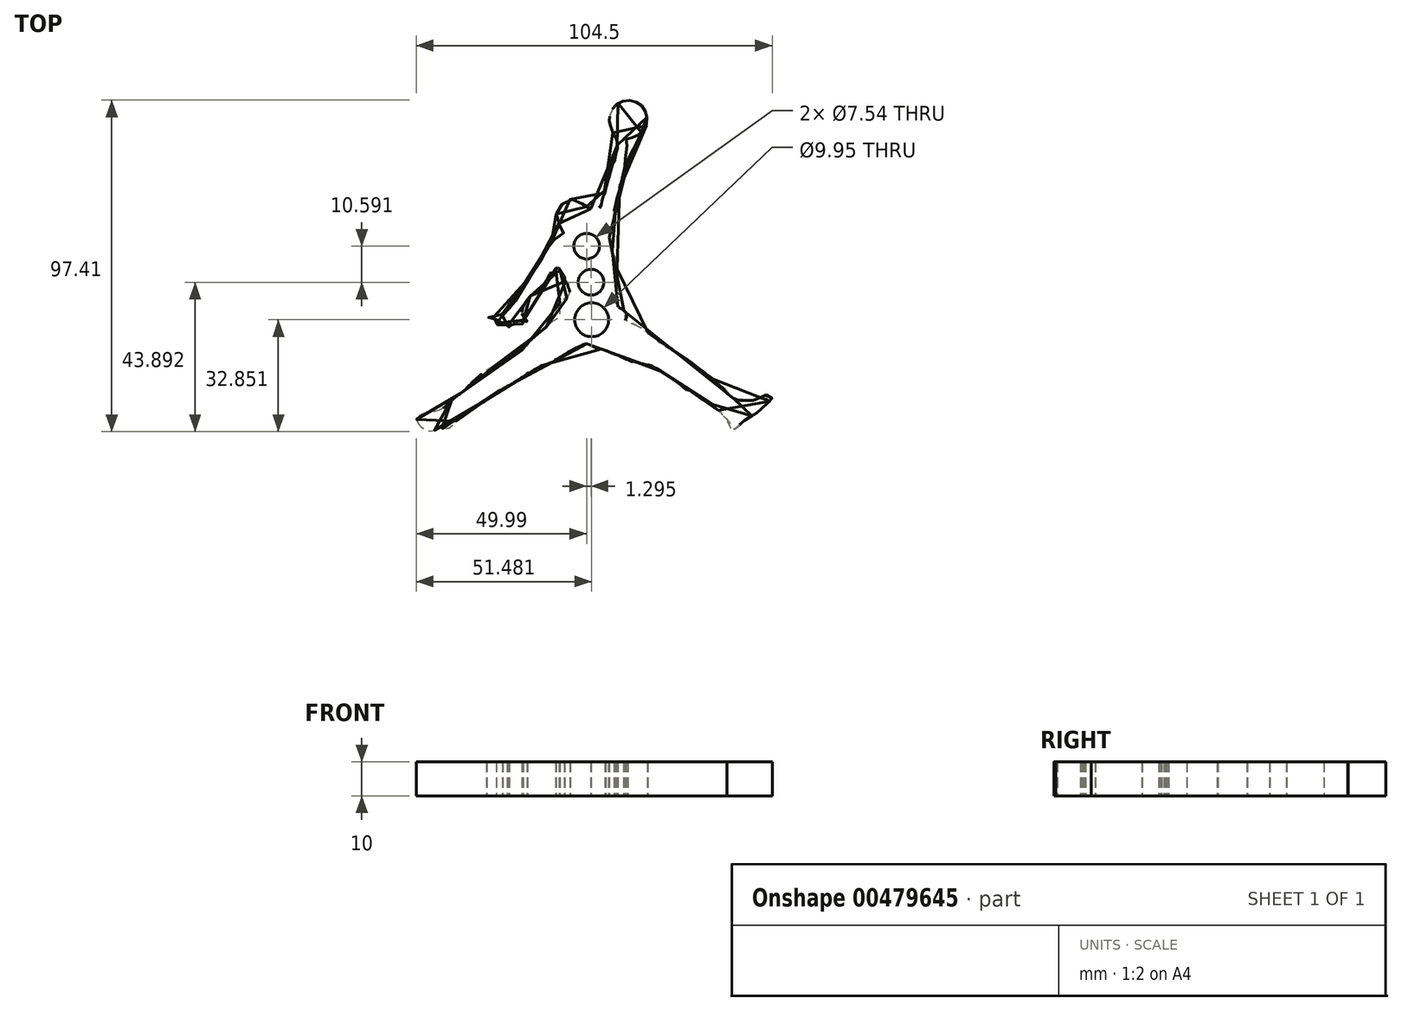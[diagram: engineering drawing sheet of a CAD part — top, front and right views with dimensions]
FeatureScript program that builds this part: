
annotation { "Feature Type Name" : "Feature", "Feature Type Description" : "" }
export const myFeature = defineFeature(function(context is Context, id is Id, definition is map)
    precondition{}
    {
        {
            var Q0;
            Q0=qCreatedBy(makeId("Top.planeOp"),FACE);
            var sketch = newSketch(context, id + "F0", { "sketchPlane" : qUnion([Q0])});
            skFitSpline(sketch, "E0", {"points": [v(0, -19.8) * mm, v(0.2, -19.83) * mm, v(0.48, -19.99) * mm, v(1.1, -20.32) * mm, v(2.32, -20.88) * mm, v(3.56, -21.27) * mm, v(5.27, -21.74) * mm, v(7.68, -22.78) * mm, v(9.68, -23.51) * mm, v(11.32, -24.32) * mm, v(13.95, -25.3) * mm, v(15.3, -25.56) * mm, v(18.19, -26.14) * mm, v(19.48, -26.44) * mm, v(19.57, -26.65) * mm, v(20.06, -26.91) * mm, v(21.05, -27.34) * mm, v(22.12, -27.94) * mm, v(23.74, -29.2) * mm, v(25.71, -30.67) * mm, v(27.3, -31.83) * mm, v(28.82, -33.03) * mm, v(29.33, -33.3) * mm, v(29.66, -33.44) * mm, v(30.19, -33.56) * mm, v(30.42, -33.56) * mm, v(31.1, -34.2) * mm, v(32.19, -34.96) * mm, v(33.13, -35.66) * mm, v(34.06, -36.37) * mm, v(34.75, -36.83) * mm, v(35.13, -36.98) * mm, v(35.58, -36.98) * mm, v(35.91, -36.98) * mm, v(36.16, -36.98) * mm, v(36.7, -37.44) * mm, v(37.25, -37.84) * mm, v(37.4, -38.04) * mm, v(37.53, -38.3) * mm, v(37.79, -38.55) * mm, v(38.11, -38.88) * mm, v(38.42, -39.16) * mm, v(38.8, -39.59) * mm, v(39.15, -39.72) * mm, v(39.3, -40) * mm, v(39.44, -40.32) * mm, v(40.42, -41.42) * mm, v(40.69, -41.76) * mm, v(41.12, -42) * mm, v(41.13, -42.31) * mm, v(41.37, -42.96) * mm, v(41.75, -43.62) * mm, v(42.58, -45) * mm, v(43.18, -45) * mm, v(44.19, -44.26) * mm, v(45.57, -43.07) * mm, v(47.18, -41.78) * mm, v(49.3, -40.67) * mm, v(51.32, -39.06) * mm, v(52.93, -37.54) * mm, v(54.5, -35.98) * mm, v(54.31, -35.5) * mm, v(53.92, -35.14) * mm, v(53.48, -34.9) * mm, v(52.87, -34.71) * mm, v(52.07, -34.83) * mm, v(51.46, -35.2) * mm, v(50.72, -35.63) * mm, v(50.03, -36.06) * mm, v(49.52, -36.26) * mm, v(48.35, -36.32) * mm, v(46.9, -36.34) * mm, v(45.76, -36.31) * mm, v(44.32, -36.3) * mm, v(43.12, -35.83) * mm, v(42.05, -34.72) * mm, v(41.47, -34.5) * mm, v(41.02, -34.03) * mm, v(40.88, -33.43) * mm, v(40.56, -33) * mm, v(39.17, -32.11) * mm, v(37.3, -30.2) * mm, v(36.82, -29.96) * mm, v(35.4, -28.76) * mm, v(33.62, -27.29) * mm, v(31.48, -25.76) * mm, v(29, -23.88) * mm, v(27.27, -22.71) * mm, v(25.08, -21.3) * mm, v(23.68, -20.35) * mm, v(23.38, -20.22) * mm, v(22.62, -20.12) * mm, v(21.98, -19.97) * mm, v(20.96, -18.83) * mm, v(19.69, -17.68) * mm, v(18.54, -16.8) * mm, v(17.36, -15.88) * mm, v(15.82, -14.96) * mm, v(14.2, -14.23) * mm, v(13, -13.6) * mm, v(11.37, -12.78) * mm, v(11.5, -12.6) * mm, v(11.63, -12.33) * mm, v(11.73, -12.03) * mm, v(11.78, -11.66) * mm, v(11.78, -11.43) * mm, v(11.72, -11.1) * mm, v(11.47, -10.57) * mm, v(11.04, -10.14) * mm, v(10.46, -9.65) * mm, v(9.6, -9.16) * mm, v(9.23, -9.02) * mm, v(8.92, -8.2) * mm, v(8.4, -7.03) * mm, v(8.55, -6.5) * mm, v(8.93, -4.45) * mm, v(9.15, -2.65) * mm, v(9.15, -0.27) * mm, v(9.04, 3.33) * mm, v(8.75, 5.3) * mm, v(7.8, 6.92) * mm, v(7.17, 8.5) * mm, v(6.73, 10.55) * mm, v(6.7, 11.32) * mm, v(6.63, 12.71) * mm, v(6.92, 13.58) * mm, v(7.53, 15) * mm, v(7.96, 16.47) * mm, v(8.12, 17.37) * mm, v(8.18, 18.32) * mm, v(8.17, 19) * mm, v(8.19, 19.73) * mm, v(8.4, 20.15) * mm, v(8.63, 20.9) * mm, v(8.65, 21.68) * mm, v(8.69, 22.57) * mm, v(9.04, 23.14) * mm, v(9.28, 23.9) * mm, v(9.63, 25.04) * mm, v(10.14, 27.67) * mm, v(10.56, 28.03) * mm, v(10.97, 28.41) * mm, v(10.97, 29.06) * mm, v(11.35, 30.86) * mm, v(11.47, 32.16) * mm, v(11.26, 32.93) * mm, v(11.38, 34.34) * mm, v(11.55, 35.53) * mm, v(11.75, 36.87) * mm, v(11.8, 37.9) * mm, v(12.08, 38.72) * mm, v(12.08, 39.7) * mm, v(11.8, 40.14) * mm, v(11.77, 40.47) * mm, v(11.97, 40.67) * mm, v(12.41, 40.67) * mm, v(13.83, 40.86) * mm, v(15.35, 41.58) * mm, v(16.46, 42.42) * mm, v(17.28, 43.69) * mm, v(17.85, 45.37) * mm, v(17.85, 46.66) * mm, v(17.7, 47.76) * mm, v(16.45, 50) * mm, v(14.85, 51.2) * mm, v(13.17, 51.76) * mm, v(11.4, 51.72) * mm, v(9.32, 51) * mm, v(7.84, 49.76) * mm, v(7.04, 48.07) * mm, v(6.52, 46.47) * mm, v(6.8, 44.8) * mm, v(7.12, 43.59) * mm, v(7.52, 42.5) * mm, v(7.92, 41.63) * mm, v(8.48, 40.63) * mm, v(8.8, 39.59) * mm, v(9, 38.7) * mm, v(8.8, 37.22) * mm, v(8.32, 35.02) * mm, v(8, 33.7) * mm, v(7.64, 33.68) * mm, v(7.49, 33.28) * mm, v(6.98, 31.54) * mm, v(6.42, 29.74) * mm, v(6.4, 29.36) * mm, v(6.52, 29.25) * mm, v(6.28, 28.69) * mm, v(5.8, 27.72) * mm, v(5.47, 26.9) * mm, v(5.43, 25.97) * mm, v(5.5, 25.32) * mm, v(4.93, 23.98) * mm, v(4.28, 21.56) * mm, v(3.93, 20.36) * mm, v(2.62, 19.25) * mm, v(1.97, 17.75) * mm, v(1.83, 18.14) * mm, v(1.6, 18.68) * mm, v(1.35, 18.93) * mm, v(1.25, 19.12) * mm, v(1.26, 19.84) * mm, v(1.16, 20) * mm, v(0.85, 20.1) * mm, v(0, 20.35) * mm, v(-0.12, 20.4) * mm, v(-0.3, 20.79) * mm, v(-0.65, 20.9) * mm, v(-0.93, 21) * mm, v(-1.4, 21.55) * mm, v(-2.02, 22.07) * mm, v(-2.8, 22.45) * mm, v(-3.7, 22.65) * mm, v(-4.58, 22.65) * mm, v(-5.6, 22.44) * mm, v(-5.99, 22.27) * mm, v(-6.86, 21.68) * mm, v(-7.56, 20.92) * mm, v(-8.27, 19.95) * mm, v(-9, 18.2) * mm, v(-8.94, 16.83) * mm, v(-8.44, 15.6) * mm, v(-7.7, 14.82) * mm, v(-7, 14.19) * mm, v(-6.7, 13.85) * mm, v(-6.6, 13.68) * mm, v(-6.76, 13.45) * mm, v(-6.84, 12.99) * mm, v(-6.96, 12.6) * mm, v(-7.42, 12.08) * mm, v(-8.13, 11.5) * mm, v(-8.53, 11.19) * mm, v(-8.97, 11.19) * mm, v(-9.5, 10.92) * mm, v(-10.2, 10.58) * mm, v(-10.93, 9.51) * mm, v(-11.95, 7.84) * mm, v(-12.98, 6.05) * mm, v(-13.52, 4.9) * mm, v(-13.7, 4.78) * mm, v(-14.25, 4.13) * mm, v(-14.77, 3.23) * mm, v(-15.14, 2.47) * mm, v(-15.35, 1.54) * mm, v(-15.93, 1.12) * mm, v(-17.56, -1.04) * mm, v(-18.35, -2.14) * mm, v(-19.01, -3.42) * mm, v(-20.12, -5.37) * mm, v(-20.55, -6.26) * mm, v(-20.93, -7.15) * mm, v(-21.08, -7.54) * mm, v(-21.83, -8.35) * mm, v(-22.7, -9.2) * mm, v(-23.65, -10.32) * mm, v(-25.58, -11.33) * mm, v(-26.46, -11.67) * mm, v(-28.16, -11.97) * mm, v(-29.17, -11.95) * mm, v(-29.43, -12.14) * mm, v(-29.32, -12.52) * mm, v(-29, -12.68) * mm, v(-27.78, -12.87) * mm, v(-26.67, -12.85) * mm, v(-25.56, -12.66) * mm, v(-24.78, -12.47) * mm, v(-24.7, -12.59) * mm, v(-24.87, -12.85) * mm, v(-25.4, -13.1) * mm, v(-25.98, -13.34) * mm, v(-26.48, -13.58) * mm, v(-26.53, -14) * mm, v(-26.24, -14.29) * mm, v(-25.72, -14.29) * mm, v(-24.7, -13.98) * mm, v(-23.6, -13.65) * mm, v(-22.87, -13.37) * mm, v(-22.96, -13.82) * mm, v(-23.2, -14.24) * mm, v(-23.36, -14.69) * mm, v(-23.05, -14.93) * mm, v(-22.32, -14.76) * mm, v(-21.54, -13.82) * mm, v(-20.95, -13.23) * mm, v(-20.53, -12.99) * mm, v(-20.12, -13.18) * mm, v(-19.86, -13.58) * mm, v(-19.18, -13.89) * mm, v(-18.45, -14) * mm, v(-17.79, -14) * mm, v(-17.43, -13.72) * mm, v(-17.38, -13.3) * mm, v(-17.64, -13.01) * mm, v(-18.33, -12.87) * mm, v(-18.7, -12.54) * mm, v(-18.92, -12) * mm, v(-18.68, -11.57) * mm, v(-18.87, -10.93) * mm, v(-18.85, -9.99) * mm, v(-18.42, -8.8) * mm, v(-17.71, -7.37) * mm, v(-17.02, -6.38) * mm, v(-16.6, -5.89) * mm, v(-15.45, -5.26) * mm, v(-13.94, -3.96) * mm, v(-12.68, -2.73) * mm, v(-11.66, -1.05) * mm, v(-10.86, 0.42) * mm, v(-10.74, 0.83) * mm, v(-10.32, 0.94) * mm, v(-9.56, 1.34) * mm, v(-9.27, 1.78) * mm, v(-8.99, 2.36) * mm, v(-8.7, 2.32) * mm, v(-8.16, 2.3) * mm, v(-7.93, 2.01) * mm, v(-7.62, 1.44) * mm, v(-7.2, 0.76) * mm, v(-6.8, 0.19) * mm, v(-6.56, -0.15) * mm, v(-6.51, -0.63) * mm, v(-6.5, -1.2) * mm, v(-6.23, -1.5) * mm, v(-5.87, -2) * mm, v(-5.69, -2.18) * mm, v(-5.6, -2.7) * mm, v(-5.39, -3.44) * mm, v(-5.2, -4.1) * mm, v(-4.96, -4.71) * mm, v(-4.88, -5.07) * mm, v(-5.35, -5.55) * mm, v(-5.75, -6.2) * mm, v(-5.9, -6.54) * mm, v(-6.45, -6.58) * mm, v(-6.95, -6.78) * mm, v(-7.52, -7.26) * mm, v(-7.82, -7.89) * mm, v(-8.02, -8.63) * mm, v(-8.02, -9.27) * mm, v(-8.07, -11.5) * mm, v(-8.53, -12.18) * mm, v(-9.13, -12.78) * mm, v(-9.73, -13.06) * mm, v(-10.45, -13.22) * mm, v(-10.95, -13.6) * mm, v(-11.33, -14.19) * mm, v(-11.53, -14.49) * mm, v(-12.87, -15.47) * mm, v(-14.13, -16.47) * mm, v(-15.42, -17.68) * mm, v(-16.6, -19.1) * mm, v(-17.56, -20.03) * mm, v(-18.21, -21.16) * mm, v(-18.58, -21.64) * mm, v(-18.96, -21.75) * mm, v(-19.47, -21.82) * mm, v(-20.07, -22.02) * mm, v(-20.92, -22.52) * mm, v(-21.49, -23.06) * mm, v(-21.94, -23.46) * mm, v(-24.7, -24.7) * mm, v(-28.08, -26.7) * mm, v(-30.64, -28.42) * mm, v(-32.43, -29.87) * mm, v(-33.58, -30.95) * mm, v(-35.47, -32.92) * mm, v(-36.76, -34.15) * mm, v(-38.14, -35.01) * mm, v(-39.62, -36.3) * mm, v(-40.97, -37.56) * mm, v(-42.2, -38.67) * mm, v(-43.45, -39.22) * mm, v(-44.68, -39.65) * mm, v(-45.7, -39.83) * mm, v(-46.8, -40.02) * mm, v(-48.3, -40.26) * mm, v(-49.8, -41.48) * mm, v(-49.93, -42.56) * mm, v(-49.26, -43.64) * mm, v(-47.97, -44.8) * mm, v(-46.76, -45.47) * mm, v(-44.93, -45.47) * mm, v(-43.58, -44.86) * mm, v(-42.36, -44.66) * mm, v(-41.07, -44.66) * mm, v(-39.86, -44.39) * mm, v(-38.98, -43.3) * mm, v(-38.37, -42.56) * mm, v(-37.76, -42.3) * mm, v(-37.02, -41.75) * mm, v(-36.27, -40.26) * mm, v(-35.33, -39.86) * mm, v(-34.51, -38.98) * mm, v(-33.77, -38.57) * mm, v(-32.55, -37.9) * mm, v(-32.14, -37.58) * mm, v(-31.84, -37.74) * mm, v(-31.3, -37.86) * mm, v(-30.89, -37.67) * mm, v(-30.39, -37.22) * mm, v(-25.67, -33.66) * mm, v(-25, -33.4) * mm, v(-22.17, -31.83) * mm, v(-19.98, -30.47) * mm, v(-17.05, -28.43) * mm, v(-15.38, -27.23) * mm, v(-13.6, -26.45) * mm, v(-9.74, -24.72) * mm, v(-7.28, -23.42) * mm, v(-4.62, -21.74) * mm, v(-2.1, -20.54) * mm, v(-0.7, -19.91) * mm, v(0, -19.8) * mm]});
            skCircle(sketch, "E1", {"center": v(0, 8.9) * mm, "radius": 3.67 * mm});
            skCircle(sketch, "E2", {"center": v(1.5, -12.74) * mm, "radius": 4.88 * mm});
            skCircle(sketch, "E3", {"center": v(1.3, -1.7) * mm, "radius": 3.67 * mm});
            skSolve(sketch);
        }
        {
            var Q0;
            Q0=makeQuery(id+"F0.imprint","IMPRINT",FACE,{"disambiguationData":[TD([[makeQuery(id+"F0.imprint","IMPRINT",EDGE,{"derivedFrom":sQuery(id+"F0.wireOp",EDGE,"E0")}),1.0]])]});
            extrude(context, id + "F1", {"entities" : qUnion([Q0]), "depth" : 10 * mm});
        }
        {
            var Q0;
            Q0=makeQuery(id+"F1.opExtrude","CAP_FACE",FACE,{"disambiguationData":[OSD([sQuery(id+"F0.wireOp",EDGE,"E0")])],"isStart":false});
            shell(context, id + "F2", {"entities" : qUnion([Q0]), "thickness" : 0.1 * mm});
        }
        {
            var Q0;
            {var subQ0=sQuery(id+"F0.wireOp",EDGE,"E1");var subQ1=sQuery(id+"F0.wireOp",EDGE,"E0");Q0=makeQuery(id+"F2.opShell","OFFSET_FACE",FACE,{"disambiguationData":[OSD([subQ1,subQ0]),TDD([makeQuery(id+"F1.opExtrude","CAP_FACE",FACE,{"disambiguationData":[OSD([subQ1,subQ0])],"isStart":false})])]});}
            extrude(context, id + "F3", {"entities" : qUnion([Q0]), "operationType" : NewBodyOperationType.REMOVE, "oppositeDirection" : true, "depth" : 25 * mm});
        }
    });
